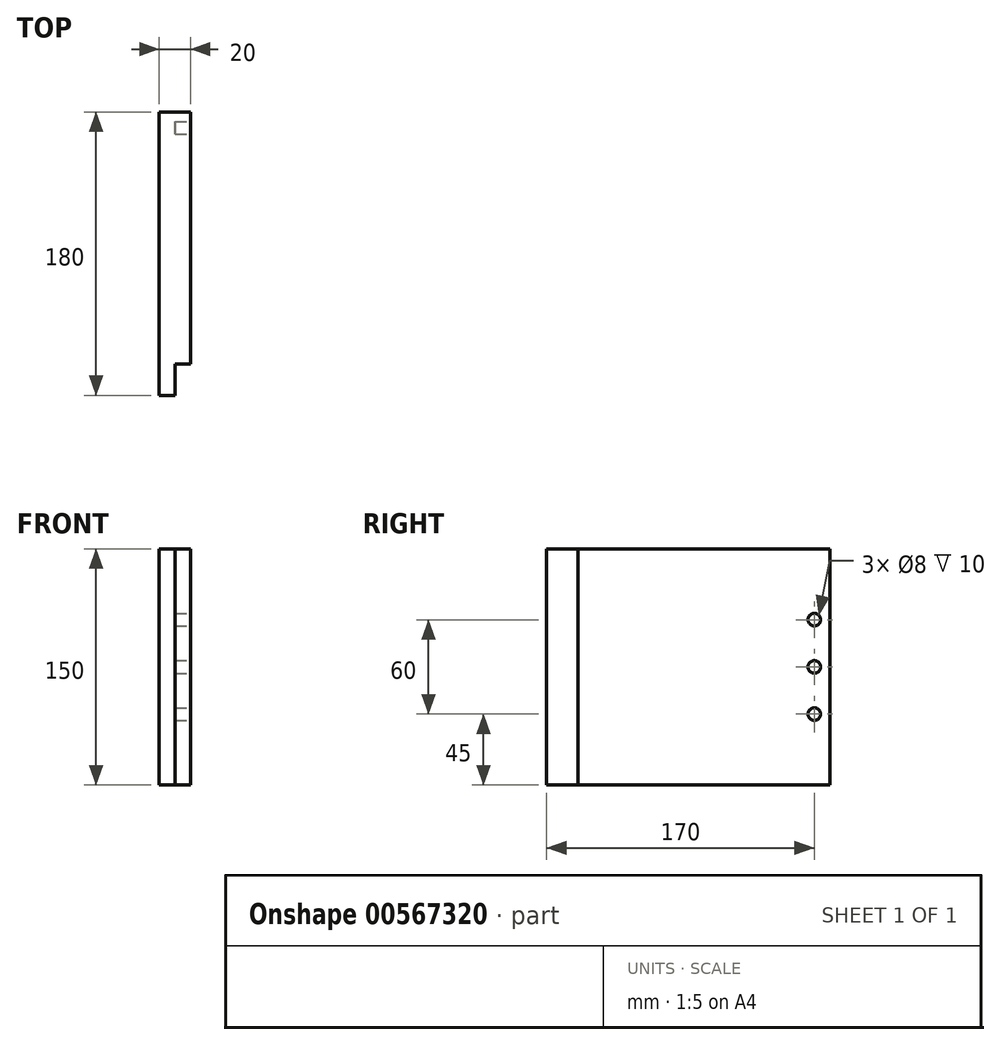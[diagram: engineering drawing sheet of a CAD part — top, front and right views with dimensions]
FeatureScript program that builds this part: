
annotation { "Feature Type Name" : "Feature", "Feature Type Description" : "" }
export const myFeature = defineFeature(function(context is Context, id is Id, definition is map)
    precondition{}
    {
        {
            var Q0;
            Q0=qCreatedBy(makeId("Front.planeOp"),FACE);
            var sketch = newSketch(context, id + "F0", { "sketchPlane" : qUnion([Q0])});
            skLineSegment(sketch, "E0.bottom", {"start": v(0, 0) * mm, "end": v(-180, 0) * mm});
            skLineSegment(sketch, "E0.top", {"start": v(0, 150) * mm, "end": v(-180, 150) * mm});
            skLineSegment(sketch, "E0.left", {"start": v(0, 0) * mm, "end": v(0, 150) * mm});
            skLineSegment(sketch, "E0.right", {"start": v(-180, 0) * mm, "end": v(-180, 150) * mm});
            skSolve(sketch);
        }
        {
            var Q0;
            Q0 = qSketchRegion(id + "F0", true);
            extrude(context, id + "F1", {"entities" : qUnion([Q0]), "depth" : 20 * mm, "offsetDistance" : 25 * mm});
        }
        {
            var Q0;
            Q0=makeQuery(id+"F1.opExtrude","CAP_FACE",FACE,{"disambiguationData":[OSD([sQuery(id+"F0.wireOp",EDGE,"E0.bottom"),sQuery(id+"F0.wireOp",EDGE,"E0.top"),sQuery(id+"F0.wireOp",EDGE,"E0.left"),sQuery(id+"F0.wireOp",EDGE,"E0.right")])],"isStart":false});
            var sketch = newSketch(context, id + "F2", { "sketchPlane" : qUnion([Q0])});
            skCircle(sketch, "E1", {"center": v(-10, 75) * mm, "radius": 4 * mm});
            skCircle(sketch, "E2", {"center": v(-10, 105) * mm, "radius": 4 * mm});
            skCircle(sketch, "E3", {"center": v(-10, 45) * mm, "radius": 4 * mm});
            skSolve(sketch);
        }
        {
            var Q0;
            Q0=makeQuery(id+"F2.imprint","IMPRINT",FACE,{"disambiguationData":[TD([[makeQuery(id+"F2.imprint","IMPRINT",EDGE,{"derivedFrom":sQuery(id+"F2.wireOp",EDGE,"E2")}),1.0]])]});
            var Q1;
            Q1=makeQuery(id+"F2.imprint","IMPRINT",FACE,{"disambiguationData":[TD([[makeQuery(id+"F2.imprint","IMPRINT",EDGE,{"derivedFrom":sQuery(id+"F2.wireOp",EDGE,"E1")}),1.0]])]});
            var Q2;
            Q2=makeQuery(id+"F2.imprint","IMPRINT",FACE,{"disambiguationData":[TD([[makeQuery(id+"F2.imprint","IMPRINT",EDGE,{"derivedFrom":sQuery(id+"F2.wireOp",EDGE,"E3")}),1.0]])]});
            extrude(context, id + "F3", {"entities" : qUnion([Q0, Q1, Q2]), "operationType" : NewBodyOperationType.REMOVE, "oppositeDirection" : true, "depth" : 10 * mm, "offsetDistance" : 25 * mm});
        }
        {
            var Q0;
            Q0=makeQuery(id+"F1.opExtrude","CAP_FACE",FACE,{"disambiguationData":[OSD([sQuery(id+"F0.wireOp",EDGE,"E0.bottom"),sQuery(id+"F0.wireOp",EDGE,"E0.top"),sQuery(id+"F0.wireOp",EDGE,"E0.left"),sQuery(id+"F0.wireOp",EDGE,"E0.right")])],"isStart":false});
            var sketch = newSketch(context, id + "F4", { "sketchPlane" : qUnion([Q0])});
            skLineSegment(sketch, "E4", {"start": v(-180, 150) * mm, "end": v(-160, 150) * mm});
            skLineSegment(sketch, "E5", {"start": v(-160, 150) * mm, "end": v(-160, 0) * mm});
            skSolve(sketch);
        }
        {
            var Q0;
            Q0=makeQuery(id+"F4.imprint","IMPRINT",FACE,{"disambiguationData":[TD([[makeQuery(id+"F4.imprint","IMPRINT",EDGE,{"derivedFrom":sQuery(id+"F4.wireOp",EDGE,"E4")}),1.0]])]});
            extrude(context, id + "F5", {"entities" : qUnion([Q0]), "operationType" : NewBodyOperationType.REMOVE, "oppositeDirection" : true, "depth" : 10 * mm, "offsetDistance" : 25 * mm});
        }
        {
            var Q0;
            Q0=makeQuery(id+"F1.opExtrude","SWEPT_BODY",BODY,{"disambiguationData":[OSD([sQuery(id+"F0.wireOp",EDGE,"E0.bottom"),sQuery(id+"F0.wireOp",EDGE,"E0.top"),sQuery(id+"F0.wireOp",EDGE,"E0.left"),sQuery(id+"F0.wireOp",EDGE,"E0.right")])]});
            var Q1;
            Q1=makeQuery(id+"F1.opExtrude","CAP_EDGE",EDGE,{"disambiguationData":[OSD([sQuery(id+"F0.wireOp",EDGE,"E0.right")])],"isStart":true});
            transform(context, id + "F6", {"entities" : qUnion([Q0]), "transformType" : TransformType.ROTATION, "transformAxis" : qUnion([Q1]), "angle" : 90 * degree, "makeCopy" : false});
        }
    });
